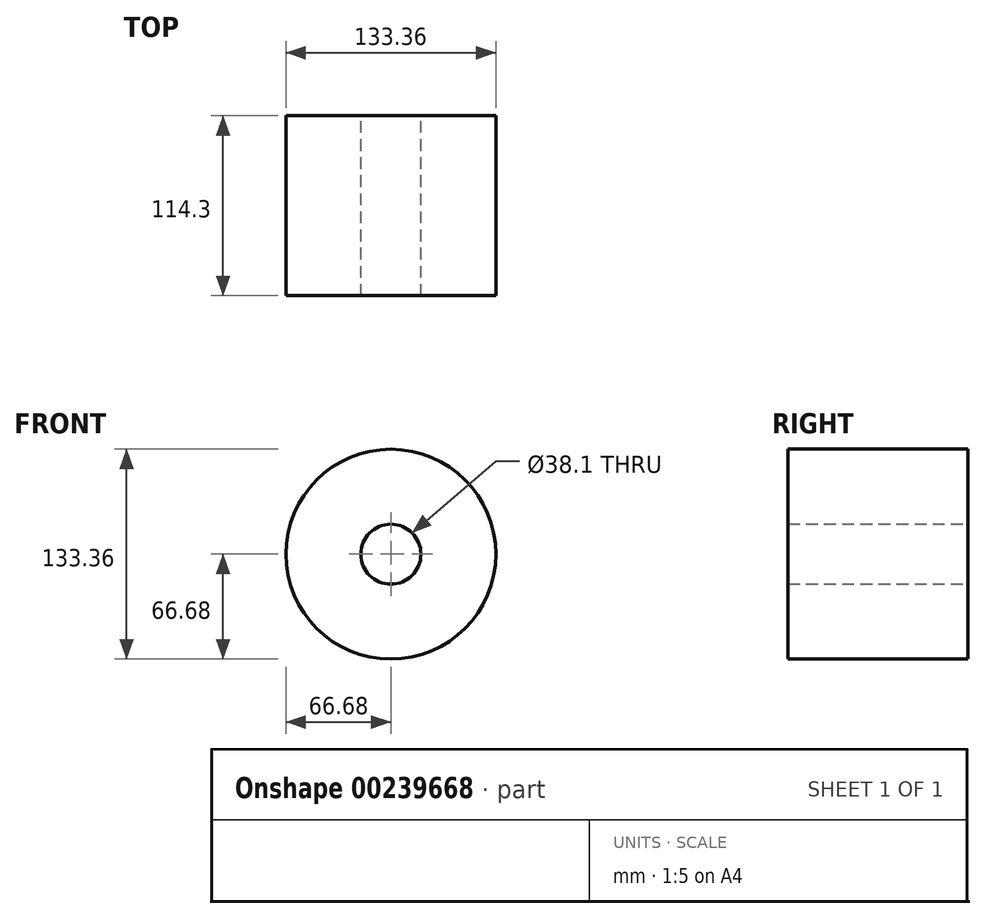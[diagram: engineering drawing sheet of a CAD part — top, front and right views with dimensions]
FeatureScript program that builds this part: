
annotation { "Feature Type Name" : "Feature", "Feature Type Description" : "" }
export const myFeature = defineFeature(function(context is Context, id is Id, definition is map)
    precondition{}
    {
        {
            var Q0;
            Q0=qCreatedBy(makeId("Front.planeOp"),FACE);
            var sketch = newSketch(context, id + "F0", { "sketchPlane" : qUnion([Q0])});
            skCircle(sketch, "E0", {"center": v(0, 0) * mm, "radius": 66.68 * mm});
            skCircle(sketch, "E1", {"center": v(0, 0) * mm, "radius": 19.05 * mm});
            skSolve(sketch);
        }
        {
            var Q0;
            Q0=makeQuery(id+"F0.imprint","IMPRINT",FACE,{"disambiguationData":[TD([[makeQuery(id+"F0.imprint","IMPRINT",EDGE,{"derivedFrom":sQuery(id+"F0.wireOp",EDGE,"E0")}),1.0]])]});
            extrude(context, id + "F1", {"entities" : qUnion([Q0]), "depth" : 114.3 * mm, "offsetDistance" : 25.4 * mm});
        }
    });
